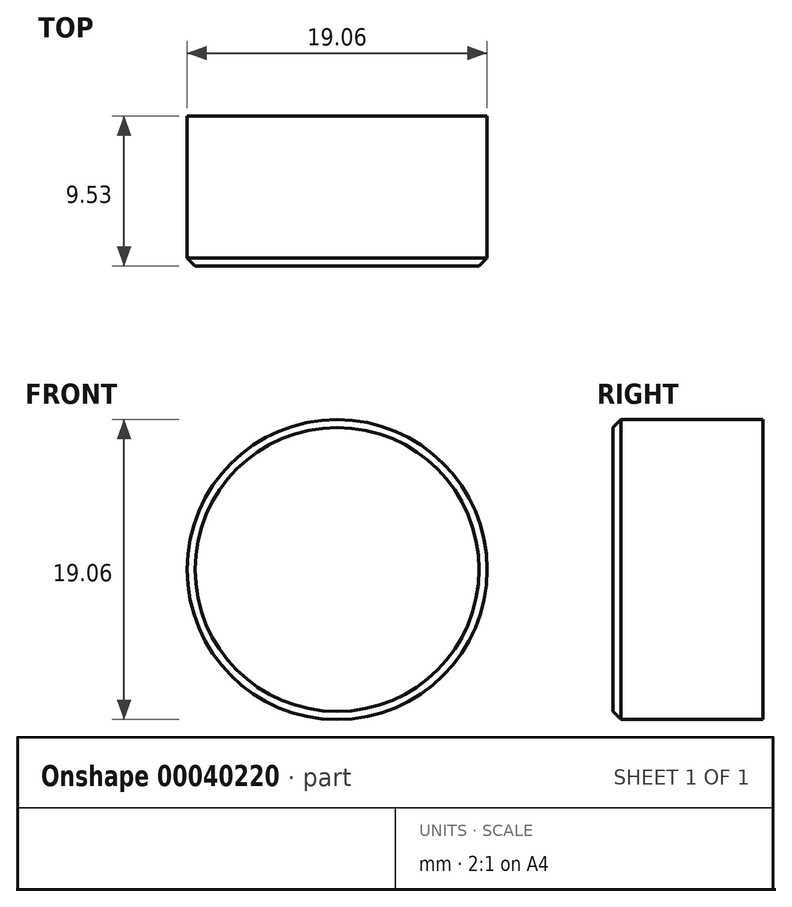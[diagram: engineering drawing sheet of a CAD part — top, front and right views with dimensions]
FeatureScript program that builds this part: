
annotation { "Feature Type Name" : "Feature", "Feature Type Description" : "" }
export const myFeature = defineFeature(function(context is Context, id is Id, definition is map)
    precondition{}
    {
        {
            var Q0;
            Q0=qCreatedBy(makeId("Front.planeOp"),FACE);
            var sketch = newSketch(context, id + "F0", { "sketchPlane" : qUnion([Q0])});
            skCircle(sketch, "E0", {"center": v(0, 0) * mm, "radius": 9.53 * mm});
            skSolve(sketch);
        }
        {
            var Q0;
            Q0 = qSketchRegion(id + "F0", true);
            extrude(context, id + "F1", {"entities" : qUnion([Q0]), "oppositeDirection" : true, "depth" : 9.52 * mm});
        }
        {
            var Q0;
            Q0=makeQuery(id+"F1.opExtrude","CAP_EDGE",EDGE,{"disambiguationData":[OSD([sQuery(id+"F0.wireOp",EDGE,"E0")])],"isStart":true});
            var Q1;
            Q1=makeQuery(id+"F2.opExtrude","CAP_EDGE",EDGE,{"disambiguationData":[OSD([sQuery(id+"FTztapcSj42NsOz_1.wireOp",EDGE,"8d4c5564-f1e7-42c2-a648-8d05bf5ee28d")])],"isStart":true});
            chamfer(context, id + "F5", {"entities" : qUnion([Q0, Q1]), "width" : 0.5 * mm, "tangentPropagation" : true});
        }
    });
